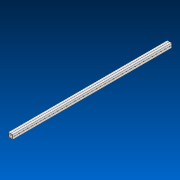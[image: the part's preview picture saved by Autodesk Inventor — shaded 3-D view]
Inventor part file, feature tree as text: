
AUTODESK INVENTOR PART (.ipt)
format: ipt  version: 2022.2 (Build 262287000, 287)  size: 798,208 bytes
history: native  units: in
note: dims shown in document units (in); Inventor stores cm internally (conversion verified against a paired STEP export)
features: other x37, extrude x1, pattern_linear x1, sketch x1, pattern_circular x1
ambient origin geometry x8: Origin, YZ Plane, XZ Plane, XY Plane, X Axis, Y Axis, Z Axis, Center Point
bodies: Solid1 (feature_tree)
feature tree (41):
  extrude  "Extrusion1"  Depth=1.0in
  other  "Work Axis1"
  pattern_linear  "Rectangular Pattern1"  Spacing1=0.0in  [1 undecoded]
  sketch  "Sketch1"  dims[d0=1.0in d1=22.0in d2=0.0in d3=14.5669in d5=1.0in]
  other  "Work Axis2"
  other  "Work Axis3"
  other  "Work Axis4"
  other  "Work Axis5"
  other  "Work Axis6"
  other  "Work Axis7"
  other  "Work Axis8"
  other  "Work Axis9"
  other  "Work Axis10"
  other  "Work Axis11"
  other  "Work Axis12"
  other  "Work Axis13"
  other  "Work Axis14"
  other  "Work Axis15"
  other  "Work Axis16"
  other  "Work Axis17"
  other  "Work Axis18"
  other  "Work Axis19"
  other  "Work Axis20"
  other  "Work Axis21"
  other  "Work Axis22"
  other  "Work Axis23"
  other  "Work Axis24"
  other  "Work Axis25"
  other  "Work Axis26"
  other  "Work Axis27"
  other  "Work Axis28"
  other  "Work Axis29"
  other  "Work Axis30"
  other  "Work Axis31"
  other  "Work Axis32"
  other  "Work Axis33"
  other  "Work Axis34"
  other  "Work Axis35"
  other  "Work Axis36"
  other  "Work Axis37"
  pattern_circular  "CirPattern2"
note: 1 required parameter value undecoded (feature->parameter linkage not recoverable at this tier; creation-order binding heuristic only, values carry confidence <= 0.55)
